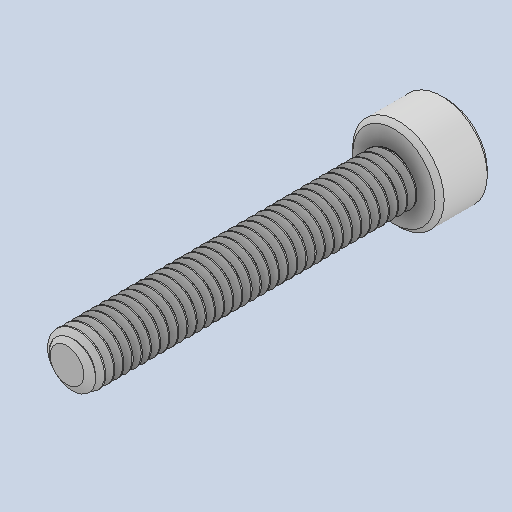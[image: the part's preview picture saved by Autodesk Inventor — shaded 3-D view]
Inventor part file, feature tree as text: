
AUTODESK INVENTOR PART (.ipt)
format: ipt  version: 2023 (Build 270158000, 158)  size: 1,128,448 bytes
history: native  units: in
note: dims shown in document units (in); Inventor stores cm internally (conversion verified against a paired STEP export)
features: chamfer x1
ambient origin geometry x8: Origin, YZ Plane, XZ Plane, XY Plane, X Axis, Y Axis, Z Axis, Center Point
bodies: Solid1 (feature_tree)
feature tree (1):
  chamfer  "Chamfer1"  [1 undecoded]
note: 1 required parameter value undecoded (feature->parameter linkage not recoverable at this tier; creation-order binding heuristic only, values carry confidence <= 0.55)
